# Revit family: Electrical_&_Lighting-Teknion-CQAMP_Routes_Power_Port-R2018
name_source: partatom
category: Electrical Fixtures
revit_build: Autodesk Revit 2018 (Build: 20190510_1515(x64)
units: mm (PartAtom-declared; Revit-internal decimal feet)

## family parameters
Always vertical = Yes
Cut with Voids When Loaded = No
Maintain Annotation Orientation = No
OmniClass Number = 23.40.20.00
OmniClass Title = General Furniture and Specialties
Part Type = Normal
Room Calculation Point = No
Round Connector Dimension = Use Diameter
Shared = Yes
Work Plane-Based = No

## types (4) — shared parameters
Apparent Load = 0 VA
Assembly Code = E2020200
Connector Description = Power Connector
Manufacturer = Teknion
Manufacturer Fax = 416.661.4586
Part Number = CQAMP
Product Documentation Link = https://www.teknion.com
Product Line = Routes
Product Page URL = https://www.teknion.com
Series = Routes
Sustainability Data = https://www.teknion.com
URL = www.teknion.com
Unit Weight URL = http://www.teknion.com
Voltage = 120 V
Warranty = http://www.teknion.com

## per-type parameters (varying)
| type | 3rd Power Cutout | Description | Desk Edge Clamp | Model | USB Cutout | Undermount |
| Triple - 3 Power, Desk Edge Clamp | 1 " | Power Port, Triple - 3 Power, Desk Edge Clamp | Yes | CQAMPT3000E___ | 0.5 " | No |
| Triple - 3 Power, Undermount | 1 " | Power Port, Triple - 3 Power, Undermount | No | CQAMPT3000U___ | 0.5 " | Yes |
| Triple - 2 Power/1 USB A&C, Desk Edge Clamp | 0.5 " | Power Port, Triple - 2 Power/1 USB A&C, Desk Edge Clamp | Yes | CQAMPT2110E___ | 1 " | No |
| Triple - 2 Power/1 USB A&C, Undermount | 0.5 " | Power Port, Triple - 2 Power/1 USB A&C, Undermount | No | CQAMPT2110U___ | 1 " | Yes |

## geometry (parser evidence)
native form markers: Sweep x3
no freeform markers — native parametric forms only
